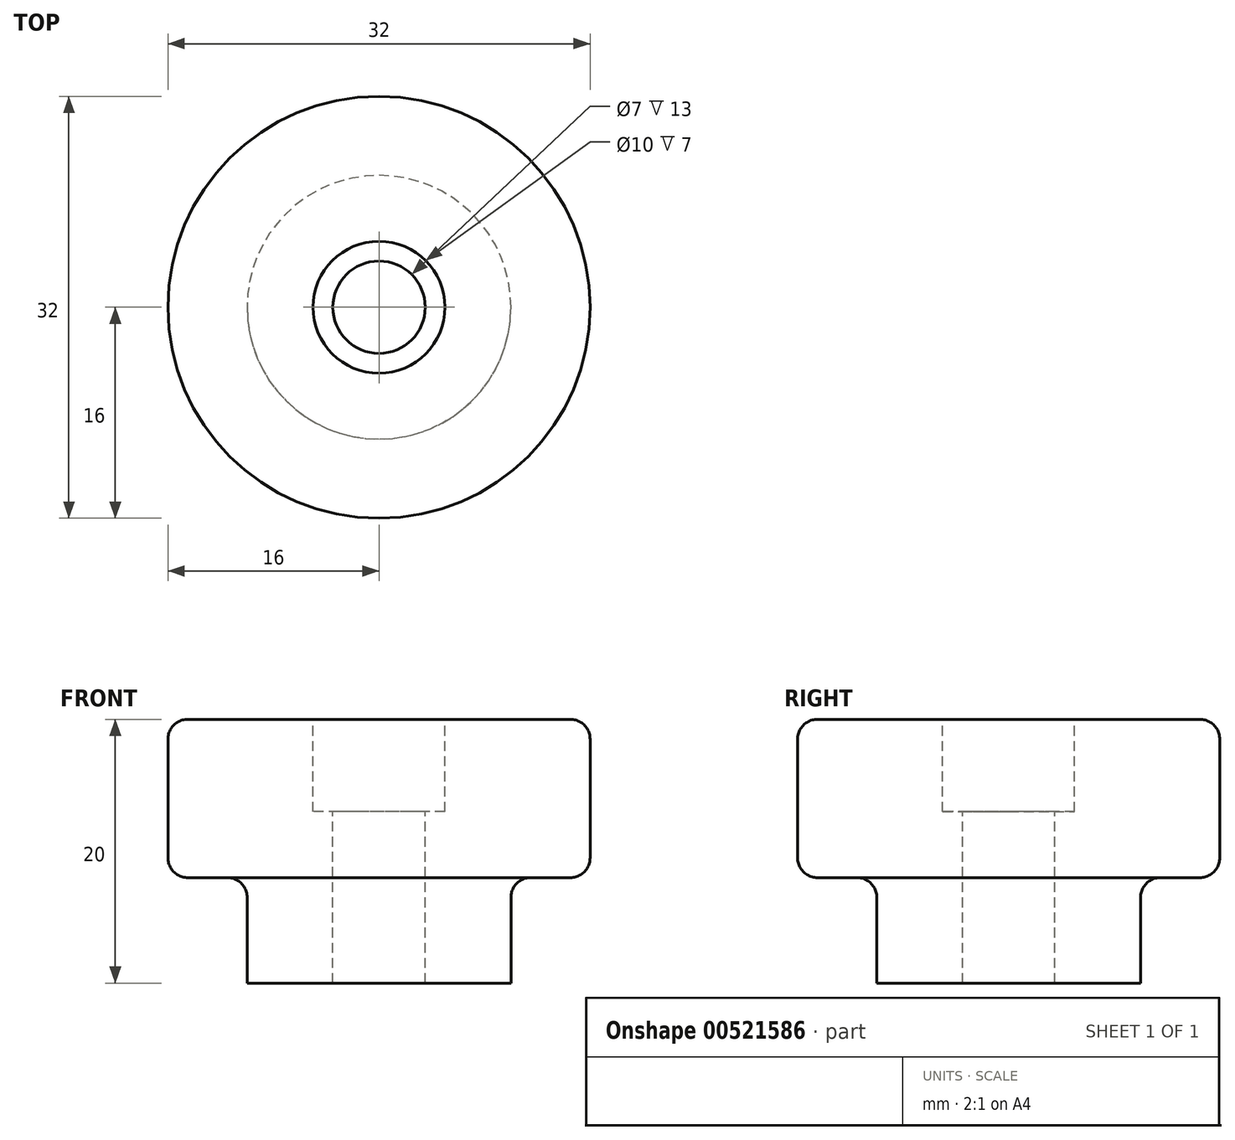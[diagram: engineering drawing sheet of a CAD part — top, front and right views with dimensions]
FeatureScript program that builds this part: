
annotation { "Feature Type Name" : "Feature", "Feature Type Description" : "" }
export const myFeature = defineFeature(function(context is Context, id is Id, definition is map)
    precondition{}
    {
        {
            var Q0;
            Q0=qCreatedBy(makeId("Top.planeOp"),FACE);
            var sketch = newSketch(context, id + "F0", { "sketchPlane" : qUnion([Q0])});
            skCircle(sketch, "E0", {"center": v(0, 0) * mm, "radius": 16 * mm});
            skSolve(sketch);
        }
        {
            var Q0;
            Q0=makeQuery(id+"F0.imprint","IMPRINT",FACE,{"disambiguationData":[TD([[makeQuery(id+"F0.imprint","IMPRINT",EDGE,{"derivedFrom":sQuery(id+"F0.wireOp",EDGE,"E0")}),1.0]])]});
            extrude(context, id + "F1", {"entities" : qUnion([Q0]), "depth" : 12 * mm, "offsetDistance" : 25 * mm});
        }
        {
            var Q0;
            Q0=makeQuery(id+"F1.opExtrude","CAP_FACE",FACE,{"disambiguationData":[OSD([sQuery(id+"F0.wireOp",EDGE,"E0")])],"isStart":true});
            var sketch = newSketch(context, id + "F2", { "sketchPlane" : qUnion([Q0])});
            skCircle(sketch, "E1", {"center": v(0, 0) * mm, "radius": 10 * mm});
            skSolve(sketch);
        }
        {
            var Q0;
            Q0=makeQuery(id+"F2.imprint","IMPRINT",FACE,{"disambiguationData":[TD([[makeQuery(id+"F2.imprint","IMPRINT",EDGE,{"derivedFrom":sQuery(id+"F2.wireOp",EDGE,"E1")}),1.0]])]});
            extrude(context, id + "F3", {"entities" : qUnion([Q0]), "operationType" : NewBodyOperationType.ADD, "depth" : 8 * mm, "offsetDistance" : 25 * mm});
        }
        {
            var Q0;
            Q0=makeQuery(id+"F1.opExtrude","CAP_FACE",FACE,{"disambiguationData":[OSD([sQuery(id+"F0.wireOp",EDGE,"E0")])],"isStart":false});
            var sketch = newSketch(context, id + "F4", { "sketchPlane" : qUnion([Q0])});
            skPoint(sketch, "E2", {"position": v(0, 0) * mm});
            skSolve(sketch);
        }
        {
            var Q0;
            Q0=sQuery(id+"F4.wireOp",VERTEX,"E2");
            var Q1;
            Q1=makeQuery(id+"F1.opExtrude","SWEPT_BODY",BODY,{"disambiguationData":[OSD([sQuery(id+"F0.wireOp",EDGE,"E0")])]});
            hole(context, id + "F5", {"style" : HoleStyle.C_BORE, "endStyle" : HoleEndStyle.THROUGH, "holeDiameter" : 7 * mm, "cBoreDiameter" : 10 * mm, "cBoreDepth" : 7 * mm, "majorDiameter" : 5 * mm, "tappedDepth" : 12 * mm, "tapClearance" : 3, "locations" : qUnion([Q0]), "scope" : qUnion([Q1])});
        }
        {
            var Q0;
            Q0=makeQuery(id+"F1.opExtrude","CAP_EDGE",EDGE,{"disambiguationData":[OSD([sQuery(id+"F0.wireOp",EDGE,"E0")])],"isStart":false});
            var Q1;
            Q1=makeQuery(id+"F1.opExtrude","CAP_EDGE",EDGE,{"disambiguationData":[OSD([sQuery(id+"F0.wireOp",EDGE,"E0")])],"isStart":true});
            var Q2;
            Q2=makeQuery(id+"F3.opExtrude","CAP_EDGE",EDGE,{"disambiguationData":[OSD([sQuery(id+"F2.wireOp",EDGE,"E1")])],"isStart":true});
            fillet(context, id + "F6", {"entities" : qUnion([Q0, Q1, Q2]), "tangentPropagation" : true, "radius" : 1.5 * mm, "defaultsChanged" : false, "vertexSettings" : []});
        }
    });
